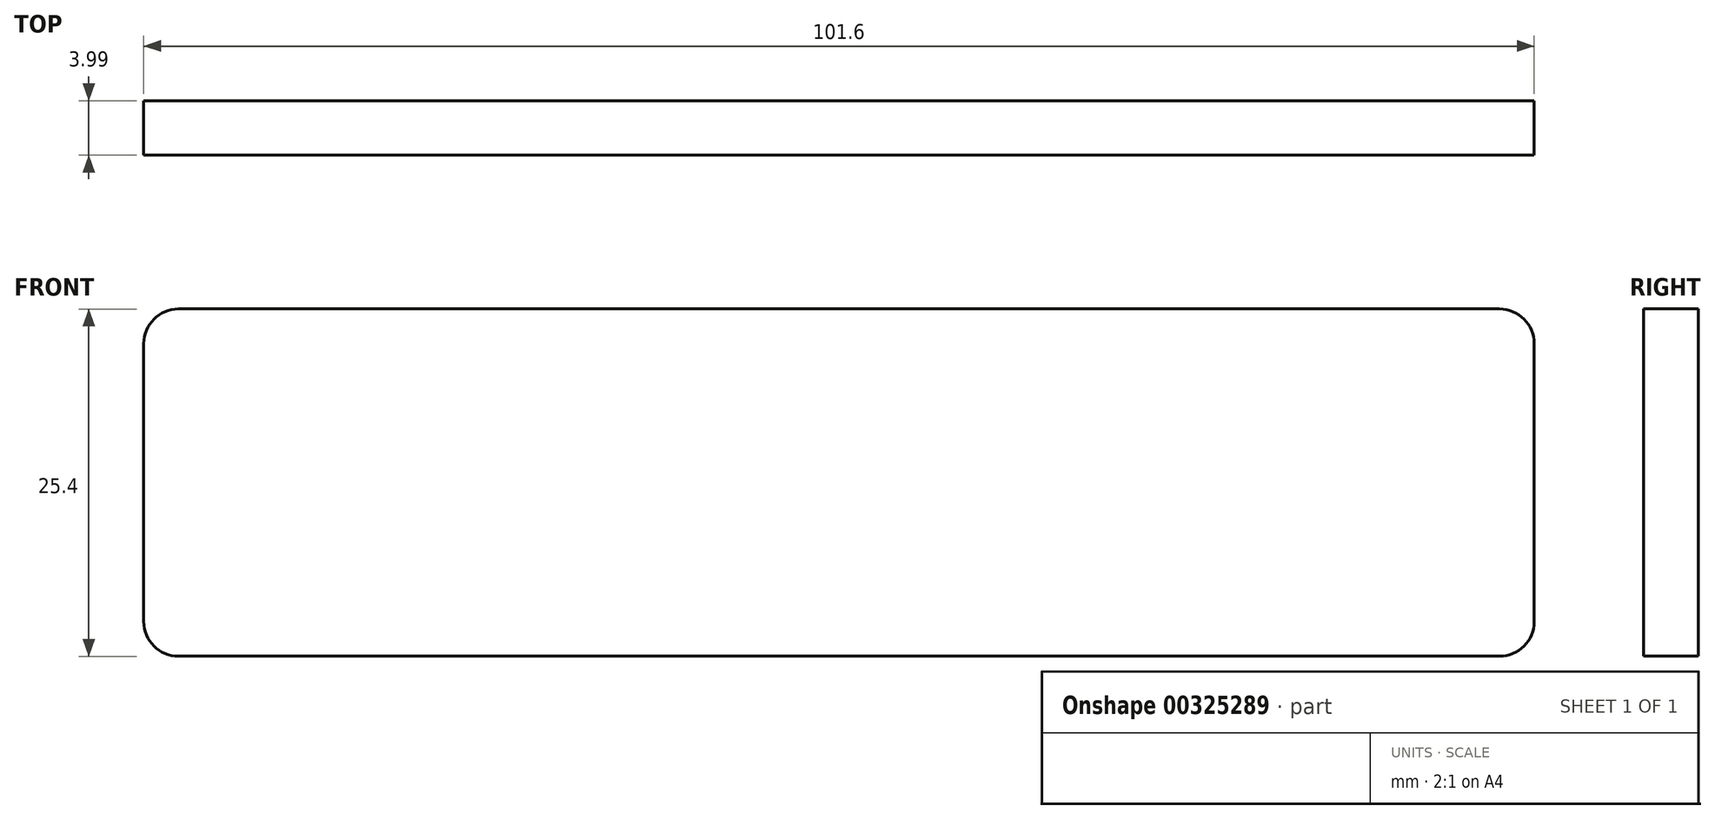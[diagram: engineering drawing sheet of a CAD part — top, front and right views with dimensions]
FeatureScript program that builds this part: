
annotation { "Feature Type Name" : "Feature", "Feature Type Description" : "" }
export const myFeature = defineFeature(function(context is Context, id is Id, definition is map)
    precondition{}
    {
        {
            var Q0;
            Q0=qCreatedBy(makeId("Front.planeOp"),FACE);
            var sketch = newSketch(context, id + "F0", { "sketchPlane" : qUnion([Q0])});
            skLineSegment(sketch, "E0", {"start": v(-49.3, 34.12) * mm, "end": v(-49.3, 8.72) * mm});
            skLineSegment(sketch, "E1", {"start": v(-49.3, 34.12) * mm, "end": v(52.3, 34.12) * mm});
            skLineSegment(sketch, "E2", {"start": v(-49.3, 8.72) * mm, "end": v(52.3, 8.72) * mm});
            skLineSegment(sketch, "E3", {"start": v(52.3, 34.12) * mm, "end": v(52.3, 8.72) * mm});
            skSolve(sketch);
        }
        {
            var Q0;
            Q0 = qSketchRegion(id + "F0", true);
            extrude(context, id + "F1", {"entities" : qUnion([Q0]), "depth" : 4 * mm});
        }
        {
            var Q0;
            Q0=makeQuery(id+"F1.opExtrude","SWEPT_EDGE",EDGE,{"disambiguationData":[OSD([sQuery(id+"F0.wireOp",EDGE,"E0"),sQuery(id+"F0.wireOp",EDGE,"E2")])]});
            fillet(context, id + "F2", {"entities" : qUnion([Q0]), "radius" : 2.54 * mm, "tangentPropagation" : true, "allowEdgeOverflow" : false});
        }
        {
            var Q0;
            Q0=makeQuery(id+"F1.opExtrude","SWEPT_EDGE",EDGE,{"disambiguationData":[OSD([sQuery(id+"F0.wireOp",EDGE,"E2"),sQuery(id+"F0.wireOp",EDGE,"E3")])]});
            fillet(context, id + "F3", {"entities" : qUnion([Q0]), "radius" : 2.54 * mm, "tangentPropagation" : true, "allowEdgeOverflow" : false});
        }
        {
            var Q0;
            Q0=makeQuery(id+"F1.opExtrude","SWEPT_EDGE",EDGE,{"disambiguationData":[OSD([sQuery(id+"F0.wireOp",EDGE,"E1"),sQuery(id+"F0.wireOp",EDGE,"E3")])]});
            fillet(context, id + "F4", {"entities" : qUnion([Q0]), "radius" : 2.54 * mm, "tangentPropagation" : true, "allowEdgeOverflow" : false});
        }
        {
            var Q0;
            Q0=makeQuery(id+"F1.opExtrude","SWEPT_EDGE",EDGE,{"disambiguationData":[OSD([sQuery(id+"F0.wireOp",EDGE,"E0"),sQuery(id+"F0.wireOp",EDGE,"E1")])]});
            fillet(context, id + "F5", {"entities" : qUnion([Q0]), "radius" : 2.54 * mm, "tangentPropagation" : true, "allowEdgeOverflow" : false});
        }
        {
            var Q0;
            Q0=qCreatedBy(makeId("Top.planeOp"),FACE);
            var sketch = newSketch(context, id + "F6", { "sketchPlane" : qUnion([Q0])});
            skCircle(sketch, "E4", {"center": v(-44.22, -2) * mm, "radius": 1.59 * mm});
            skCircle(sketch, "E5", {"center": v(47.22, -2) * mm, "radius": 1.59 * mm});
            skSolve(sketch);
        }
        {
            var Q0;
            Q0 = qSketchRegion(id + "F6", true);
            var Q1;
            Q1=makeQuery(id+"F1.opExtrude","SWEPT_FACE",FACE,{"disambiguationData":[OSD([sQuery(id+"F0.wireOp",EDGE,"E2")])]});
            extrude(context, id + "F7", {"entities" : qUnion([Q0]), "operationType" : NewBodyOperationType.REMOVE, "endBound" : BoundingType.UP_TO_SURFACE, "endBoundEntityFace" : qUnion([Q1]), "depth" : 25.4 * mm, "hasSecondDirection" : true, "secondDirectionOppositeDirection" : false, "secondDirectionDepth" : 3.17 * mm});
        }
    });
